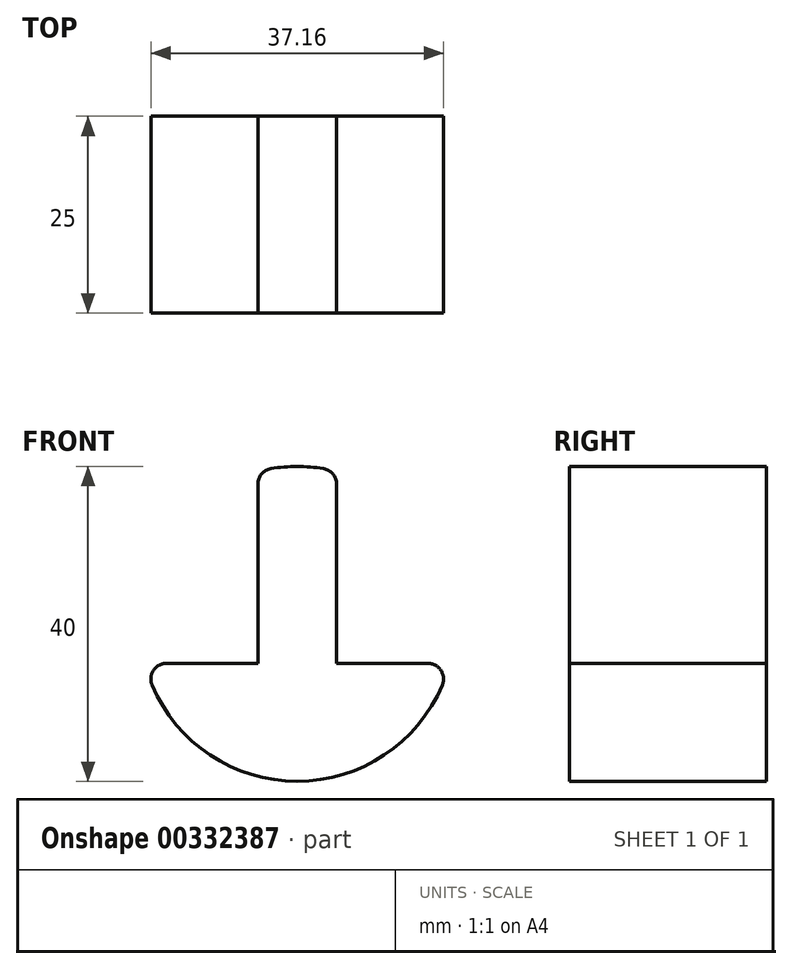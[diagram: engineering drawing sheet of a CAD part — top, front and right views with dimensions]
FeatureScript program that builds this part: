
annotation { "Feature Type Name" : "Feature", "Feature Type Description" : "" }
export const myFeature = defineFeature(function(context is Context, id is Id, definition is map)
    precondition{}
    {
        {
            var Q0;
            Q0=qCreatedBy(makeId("Front.planeOp"),FACE);
            var sketch = newSketch(context, id + "F0", { "sketchPlane" : qUnion([Q0])});
            skArc(sketch, "E0", {"start": v(3.33, 19.72) * mm, "mid": v(0, 20) * mm, "end": v(-3.33, 19.72) * mm});
            skLineSegment(sketch, "E1", {"start": v(5, 17.75) * mm, "end": v(5, -5) * mm});
            skLineSegment(sketch, "E2", {"start": v(5, -5) * mm, "end": v(16.58, -5) * mm});
            skLineSegment(sketch, "E3", {"start": v(-5, 17.75) * mm, "end": v(-5, -5) * mm});
            skLineSegment(sketch, "E4", {"start": v(-5, -5) * mm, "end": v(-16.58, -5) * mm});
            skArc(sketch, "E5.trimOffspring", {"start": v(-18.43, -7.78) * mm, "mid": v(0, -20) * mm, "end": v(18.43, -7.78) * mm});
            skPoint(sketch, "E6.visualSharp", {"position": v(-19.36, -5) * mm});
            skArc(sketch, "E6.filletArc", {"start": v(-16.58, -5) * mm, "mid": v(-18.25, -5.9) * mm, "end": v(-18.43, -7.78) * mm});
            skPoint(sketch, "E7.visualSharp", {"position": v(19.36, -5) * mm});
            skArc(sketch, "E7.filletArc", {"start": v(18.43, -7.78) * mm, "mid": v(18.25, -5.9) * mm, "end": v(16.58, -5) * mm});
            skPoint(sketch, "E8.visualSharp", {"position": v(5, 19.36) * mm});
            skArc(sketch, "E8.filletArc", {"start": v(5, 17.75) * mm, "mid": v(4.53, 19.04) * mm, "end": v(3.33, 19.72) * mm});
            skPoint(sketch, "E9.visualSharp", {"position": v(-5, 19.36) * mm});
            skArc(sketch, "E9.filletArc", {"start": v(-3.33, 19.72) * mm, "mid": v(-4.53, 19.04) * mm, "end": v(-5, 17.75) * mm});
            skSolve(sketch);
        }
        {
            var Q0;
            Q0=makeQuery(id+"F0.imprint","IMPRINT",FACE,{"disambiguationData":[TD([[makeQuery(id+"F0.imprint","IMPRINT",EDGE,{"derivedFrom":sQuery(id+"F0.wireOp",EDGE,"E0")}),1.0]])]});
            extrude(context, id + "F1", {"entities" : qUnion([Q0]), "depth" : 25 * mm});
        }
    });
